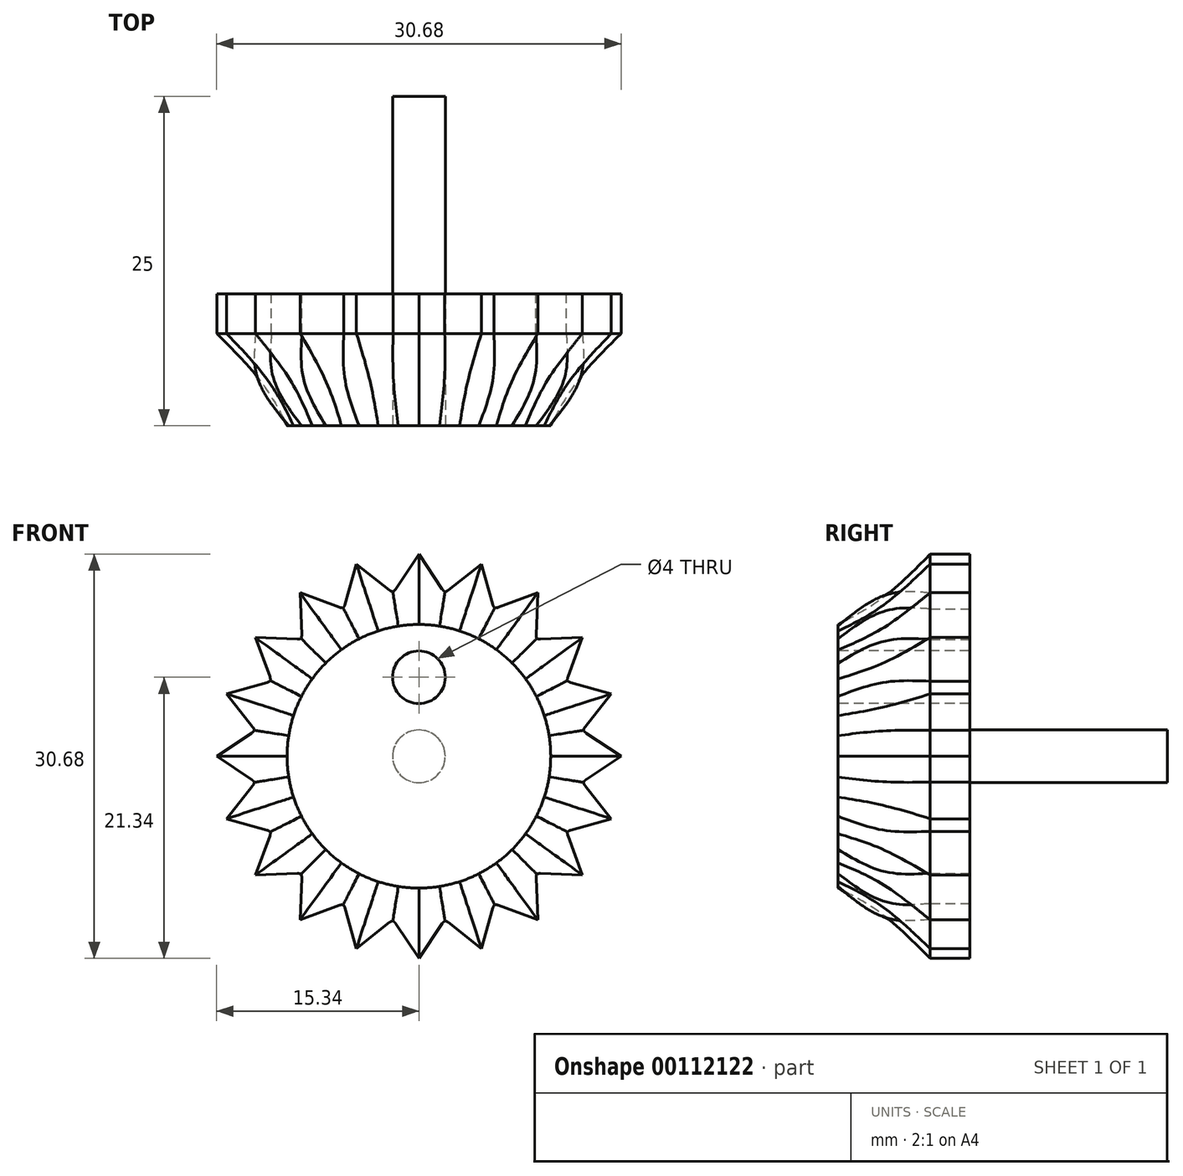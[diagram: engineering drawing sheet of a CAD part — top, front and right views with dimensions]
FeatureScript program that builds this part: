
annotation { "Feature Type Name" : "Feature", "Feature Type Description" : "" }
export const myFeature = defineFeature(function(context is Context, id is Id, definition is map)
    precondition{}
    {
        {
            var Q0;
            Q0=qCreatedBy(makeId("Front.planeOp"),FACE);
            var sketch = newSketch(context, id + "F0", { "sketchPlane" : qUnion([Q0])});
            skCircle(sketch, "E0", {"center": v(0, 0) * mm, "radius": 12.5 * mm, "construction": true});
            skLineSegment(sketch, "E1", {"start": v(-2, 12.34) * mm, "end": v(0, 15.34) * mm});
            skLineSegment(sketch, "E2", {"start": v(0, 15.34) * mm, "end": v(2, 12.34) * mm});
            skLineSegment(sketch, "E3", {"start": v(2, 12.34) * mm, "end": v(-2, 12.34) * mm, "construction": true});
            skLineSegment(sketch, "E4.1.0", {"start": v(-5.72, 11.12) * mm, "end": v(-4.74, 14.59) * mm});
            skLineSegment(sketch, "E4.1.1", {"start": v(-4.74, 14.59) * mm, "end": v(-1.91, 12.35) * mm});
            skLineSegment(sketch, "E4.2.0", {"start": v(-8.87, 8.8) * mm, "end": v(-9.02, 12.4) * mm});
            skLineSegment(sketch, "E4.2.1", {"start": v(-9.02, 12.4) * mm, "end": v(-5.63, 11.16) * mm});
            skLineSegment(sketch, "E4.3.0", {"start": v(-11.16, 5.63) * mm, "end": v(-12.4, 9.02) * mm});
            skLineSegment(sketch, "E4.3.1", {"start": v(-12.4, 9.02) * mm, "end": v(-8.8, 8.87) * mm});
            skLineSegment(sketch, "E4.4.0", {"start": v(-12.35, 1.91) * mm, "end": v(-14.59, 4.74) * mm});
            skLineSegment(sketch, "E4.4.1", {"start": v(-14.59, 4.74) * mm, "end": v(-11.12, 5.72) * mm});
            skLineSegment(sketch, "E4.5.0", {"start": v(-12.34, -2) * mm, "end": v(-15.34, 0) * mm});
            skLineSegment(sketch, "E4.5.1", {"start": v(-15.34, 0) * mm, "end": v(-12.34, 2) * mm});
            skLineSegment(sketch, "E4.6.0", {"start": v(-11.12, -5.72) * mm, "end": v(-14.59, -4.74) * mm});
            skLineSegment(sketch, "E4.6.1", {"start": v(-14.59, -4.74) * mm, "end": v(-12.35, -1.91) * mm});
            skLineSegment(sketch, "E4.7.0", {"start": v(-8.8, -8.87) * mm, "end": v(-12.4, -9.02) * mm});
            skLineSegment(sketch, "E4.7.1", {"start": v(-12.4, -9.02) * mm, "end": v(-11.16, -5.63) * mm});
            skLineSegment(sketch, "E4.8.0", {"start": v(-5.63, -11.16) * mm, "end": v(-9.02, -12.4) * mm});
            skLineSegment(sketch, "E4.8.1", {"start": v(-9.02, -12.4) * mm, "end": v(-8.87, -8.8) * mm});
            skLineSegment(sketch, "E4.9.0", {"start": v(-1.91, -12.35) * mm, "end": v(-4.74, -14.59) * mm});
            skLineSegment(sketch, "E4.9.1", {"start": v(-4.74, -14.59) * mm, "end": v(-5.72, -11.12) * mm});
            skLineSegment(sketch, "E5.1.10.0", {"start": v(2, -12.34) * mm, "end": v(0, -15.34) * mm});
            skLineSegment(sketch, "E5.3.10.0", {"start": v(0, -15.34) * mm, "end": v(-2, -12.34) * mm});
            skLineSegment(sketch, "E6.1.11.0", {"start": v(5.72, -11.12) * mm, "end": v(4.74, -14.59) * mm});
            skLineSegment(sketch, "E6.3.11.0", {"start": v(4.74, -14.59) * mm, "end": v(1.91, -12.35) * mm});
            skLineSegment(sketch, "E7.1.12.0", {"start": v(8.87, -8.8) * mm, "end": v(9.02, -12.4) * mm});
            skLineSegment(sketch, "E7.3.12.0", {"start": v(9.02, -12.4) * mm, "end": v(5.63, -11.16) * mm});
            skLineSegment(sketch, "E7.1.13.0", {"start": v(11.16, -5.63) * mm, "end": v(12.4, -9.02) * mm});
            skLineSegment(sketch, "E7.3.13.0", {"start": v(12.4, -9.02) * mm, "end": v(8.8, -8.87) * mm});
            skLineSegment(sketch, "E8.1.14.0", {"start": v(12.35, -1.91) * mm, "end": v(14.59, -4.74) * mm});
            skLineSegment(sketch, "E8.3.14.0", {"start": v(14.59, -4.74) * mm, "end": v(11.12, -5.72) * mm});
            skLineSegment(sketch, "E8.1.15.0", {"start": v(12.34, 2) * mm, "end": v(15.34, 0) * mm});
            skLineSegment(sketch, "E8.3.15.0", {"start": v(15.34, 0) * mm, "end": v(12.34, -2) * mm});
            skLineSegment(sketch, "E8.1.16.0", {"start": v(11.12, 5.72) * mm, "end": v(14.59, 4.74) * mm});
            skLineSegment(sketch, "E8.3.16.0", {"start": v(14.59, 4.74) * mm, "end": v(12.35, 1.91) * mm});
            skLineSegment(sketch, "E8.1.17.0", {"start": v(8.8, 8.87) * mm, "end": v(12.4, 9.02) * mm});
            skLineSegment(sketch, "E8.3.17.0", {"start": v(12.4, 9.02) * mm, "end": v(11.16, 5.63) * mm});
            skLineSegment(sketch, "E8.1.18.0", {"start": v(5.63, 11.16) * mm, "end": v(9.02, 12.4) * mm});
            skLineSegment(sketch, "E8.3.18.0", {"start": v(9.02, 12.4) * mm, "end": v(8.87, 8.8) * mm});
            skLineSegment(sketch, "E8.1.19.0", {"start": v(1.91, 12.35) * mm, "end": v(4.74, 14.59) * mm});
            skLineSegment(sketch, "E8.3.19.0", {"start": v(4.74, 14.59) * mm, "end": v(5.72, 11.12) * mm});
            skSolve(sketch);
        }
        {
            var Q0;
            Q0=qSketchRegion(id+"F0",true);
            extrude(context, id + "F1", {"entities" : qUnion([Q0]), "depth" : 3 * mm});
        }
        {
            var Q0;
            Q0=makeQuery(id+"F1.opExtrude","CAP_FACE",FACE,{"disambiguationData":[OSD([sQuery(id+"F0.wireOp",EDGE,"fbJdyaIG-X2Uv-iruu-1M7H-KIjKJSGYAYfz"),sQuery(id+"F0.wireOp",EDGE,"E1"),sQuery(id+"F0.wireOp",EDGE,"E2"),sQuery(id+"F0.wireOp",EDGE,"E4.1.0"),sQuery(id+"F0.wireOp",EDGE,"E4.1.1"),sQuery(id+"F0.wireOp",EDGE,"E4.2.0"),sQuery(id+"F0.wireOp",EDGE,"E4.2.1"),sQuery(id+"F0.wireOp",EDGE,"E4.3.0"),sQuery(id+"F0.wireOp",EDGE,"E4.3.1"),sQuery(id+"F0.wireOp",EDGE,"E4.4.0"),sQuery(id+"F0.wireOp",EDGE,"E4.4.1"),sQuery(id+"F0.wireOp",EDGE,"E4.5.0"),sQuery(id+"F0.wireOp",EDGE,"E4.5.1"),sQuery(id+"F0.wireOp",EDGE,"E4.6.0"),sQuery(id+"F0.wireOp",EDGE,"E4.6.1"),sQuery(id+"F0.wireOp",EDGE,"E4.7.0"),sQuery(id+"F0.wireOp",EDGE,"E4.7.1"),sQuery(id+"F0.wireOp",EDGE,"E4.8.0"),sQuery(id+"F0.wireOp",EDGE,"E4.8.1"),sQuery(id+"F0.wireOp",EDGE,"E4.9.0"),sQuery(id+"F0.wireOp",EDGE,"E4.9.1"),sQuery(id+"F0.wireOp",EDGE,"E4.10.0"),sQuery(id+"F0.wireOp",EDGE,"E4.10.1"),sQuery(id+"F0.wireOp",EDGE,"E4.11.0"),sQuery(id+"F0.wireOp",EDGE,"E4.11.1"),sQuery(id+"F0.wireOp",EDGE,"E4.12.0"),sQuery(id+"F0.wireOp",EDGE,"E4.12.1"),sQuery(id+"F0.wireOp",EDGE,"E4.13.0"),sQuery(id+"F0.wireOp",EDGE,"E4.13.1"),sQuery(id+"F0.wireOp",EDGE,"E4.14.0"),sQuery(id+"F0.wireOp",EDGE,"E4.14.1"),sQuery(id+"F0.wireOp",EDGE,"E4.15.0"),sQuery(id+"F0.wireOp",EDGE,"E4.15.1")])],"isStart":true});
            var sketch = newSketch(context, id + "F2", { "sketchPlane" : qUnion([Q0])});
            skCircle(sketch, "E9", {"center": v(0, 0) * mm, "radius": 2 * mm});
            skSolve(sketch);
        }
        {
            var Q0;
            Q0=qSketchRegion(id+"F2",true);
            extrude(context, id + "F3", {"entities" : qUnion([Q0]), "operationType" : NewBodyOperationType.ADD, "depth" : 15 * mm});
        }
        {
            var Q0;
            Q0=makeQuery(id+"F1.opExtrude","CAP_FACE",FACE,{"disambiguationData":[OSD([sQuery(id+"F0.wireOp",EDGE,"E1"),sQuery(id+"F0.wireOp",EDGE,"E2"),sQuery(id+"F0.wireOp",EDGE,"E4.1.0"),sQuery(id+"F0.wireOp",EDGE,"E4.1.1"),sQuery(id+"F0.wireOp",EDGE,"E4.2.0"),sQuery(id+"F0.wireOp",EDGE,"E4.2.1"),sQuery(id+"F0.wireOp",EDGE,"E4.3.0"),sQuery(id+"F0.wireOp",EDGE,"E4.3.1"),sQuery(id+"F0.wireOp",EDGE,"E4.4.0"),sQuery(id+"F0.wireOp",EDGE,"E4.4.1"),sQuery(id+"F0.wireOp",EDGE,"E4.5.0"),sQuery(id+"F0.wireOp",EDGE,"E4.5.1"),sQuery(id+"F0.wireOp",EDGE,"E4.6.0"),sQuery(id+"F0.wireOp",EDGE,"E4.6.1"),sQuery(id+"F0.wireOp",EDGE,"E4.7.0"),sQuery(id+"F0.wireOp",EDGE,"E4.7.1"),sQuery(id+"F0.wireOp",EDGE,"E4.8.0"),sQuery(id+"F0.wireOp",EDGE,"E4.8.1"),sQuery(id+"F0.wireOp",EDGE,"E4.9.0"),sQuery(id+"F0.wireOp",EDGE,"E4.9.1"),sQuery(id+"F0.wireOp",EDGE,"E5.1.10.0"),sQuery(id+"F0.wireOp",EDGE,"E5.3.10.0"),sQuery(id+"F0.wireOp",EDGE,"E6.1.11.0"),sQuery(id+"F0.wireOp",EDGE,"E6.3.11.0"),sQuery(id+"F0.wireOp",EDGE,"E7.1.12.0"),sQuery(id+"F0.wireOp",EDGE,"E7.3.12.0"),sQuery(id+"F0.wireOp",EDGE,"E7.1.13.0"),sQuery(id+"F0.wireOp",EDGE,"E7.3.13.0"),sQuery(id+"F0.wireOp",EDGE,"E8.1.14.0"),sQuery(id+"F0.wireOp",EDGE,"E8.3.14.0"),sQuery(id+"F0.wireOp",EDGE,"E8.1.15.0"),sQuery(id+"F0.wireOp",EDGE,"E8.3.15.0"),sQuery(id+"F0.wireOp",EDGE,"E8.1.16.0"),sQuery(id+"F0.wireOp",EDGE,"E8.3.16.0"),sQuery(id+"F0.wireOp",EDGE,"E8.1.17.0"),sQuery(id+"F0.wireOp",EDGE,"E8.3.17.0"),sQuery(id+"F0.wireOp",EDGE,"E8.1.18.0"),sQuery(id+"F0.wireOp",EDGE,"E8.3.18.0"),sQuery(id+"F0.wireOp",EDGE,"E8.1.19.0"),sQuery(id+"F0.wireOp",EDGE,"E8.3.19.0"),sQuery(id+"F0.wireOp",EDGE,"kuZlPc9k-eGlJ-LJDZ-wCxi-x52hGT55WUVo")])],"isStart":false});
            cPlane(context, id + "F4", {"entities" : qUnion([Q0]), "cplaneType" : CPlaneType.OFFSET, "offset" : 3 * mm, "width" : 150 * mm, "height" : 150 * mm});
        }
        {
            var Q0;
            Q0=qCreatedBy(id+"F4.planeOp",FACE);
            var sketch = newSketch(context, id + "F5", { "sketchPlane" : qUnion([Q0])});
            skCircle(sketch, "E10", {"center": v(0, 0) * mm, "radius": 12.5 * mm});
            skSolve(sketch);
        }
        {
            var Q0;
            Q0=makeQuery(id+"F1.opExtrude","CAP_FACE",FACE,{"disambiguationData":[OSD([sQuery(id+"F0.wireOp",EDGE,"E1"),sQuery(id+"F0.wireOp",EDGE,"E2"),sQuery(id+"F0.wireOp",EDGE,"E4.1.0"),sQuery(id+"F0.wireOp",EDGE,"E4.1.1"),sQuery(id+"F0.wireOp",EDGE,"E4.2.0"),sQuery(id+"F0.wireOp",EDGE,"E4.2.1"),sQuery(id+"F0.wireOp",EDGE,"E4.3.0"),sQuery(id+"F0.wireOp",EDGE,"E4.3.1"),sQuery(id+"F0.wireOp",EDGE,"E4.4.0"),sQuery(id+"F0.wireOp",EDGE,"E4.4.1"),sQuery(id+"F0.wireOp",EDGE,"E4.5.0"),sQuery(id+"F0.wireOp",EDGE,"E4.5.1"),sQuery(id+"F0.wireOp",EDGE,"E4.6.0"),sQuery(id+"F0.wireOp",EDGE,"E4.6.1"),sQuery(id+"F0.wireOp",EDGE,"E4.7.0"),sQuery(id+"F0.wireOp",EDGE,"E4.7.1"),sQuery(id+"F0.wireOp",EDGE,"E4.8.0"),sQuery(id+"F0.wireOp",EDGE,"E4.8.1"),sQuery(id+"F0.wireOp",EDGE,"E4.9.0"),sQuery(id+"F0.wireOp",EDGE,"E4.9.1"),sQuery(id+"F0.wireOp",EDGE,"E5.1.10.0"),sQuery(id+"F0.wireOp",EDGE,"E5.3.10.0"),sQuery(id+"F0.wireOp",EDGE,"E6.1.11.0"),sQuery(id+"F0.wireOp",EDGE,"E6.3.11.0"),sQuery(id+"F0.wireOp",EDGE,"E7.1.12.0"),sQuery(id+"F0.wireOp",EDGE,"E7.3.12.0"),sQuery(id+"F0.wireOp",EDGE,"E7.1.13.0"),sQuery(id+"F0.wireOp",EDGE,"E7.3.13.0"),sQuery(id+"F0.wireOp",EDGE,"E8.1.14.0"),sQuery(id+"F0.wireOp",EDGE,"E8.3.14.0"),sQuery(id+"F0.wireOp",EDGE,"E8.1.15.0"),sQuery(id+"F0.wireOp",EDGE,"E8.3.15.0"),sQuery(id+"F0.wireOp",EDGE,"E8.1.16.0"),sQuery(id+"F0.wireOp",EDGE,"E8.3.16.0"),sQuery(id+"F0.wireOp",EDGE,"E8.1.17.0"),sQuery(id+"F0.wireOp",EDGE,"E8.3.17.0"),sQuery(id+"F0.wireOp",EDGE,"E8.1.18.0"),sQuery(id+"F0.wireOp",EDGE,"E8.3.18.0"),sQuery(id+"F0.wireOp",EDGE,"E8.1.19.0"),sQuery(id+"F0.wireOp",EDGE,"E8.3.19.0"),sQuery(id+"F0.wireOp",EDGE,"kuZlPc9k-eGlJ-LJDZ-wCxi-x52hGT55WUVo")])],"isStart":false});
            var sketch = newSketch(context, id + "F6", { "sketchPlane" : qUnion([Q0])});
            skLineSegment(sketch, "E11.0.0", {"start": v(-4.74, -14.59) * mm, "end": v(-1.96, -12.4) * mm});
            skLineSegment(sketch, "E11.0.1", {"start": v(-1.96, -12.4) * mm, "end": v(0, -15.34) * mm});
            skLineSegment(sketch, "E11.0.2", {"start": v(0, -15.34) * mm, "end": v(1.96, -12.4) * mm});
            skLineSegment(sketch, "E11.0.3", {"start": v(1.96, -12.4) * mm, "end": v(4.74, -14.59) * mm});
            skLineSegment(sketch, "E11.0.4", {"start": v(4.74, -14.59) * mm, "end": v(5.7, -11.18) * mm});
            skLineSegment(sketch, "E11.0.5", {"start": v(5.7, -11.18) * mm, "end": v(9.02, -12.4) * mm});
            skLineSegment(sketch, "E11.0.6", {"start": v(9.02, -12.4) * mm, "end": v(8.87, -8.87) * mm});
            skLineSegment(sketch, "E11.0.7", {"start": v(8.87, -8.87) * mm, "end": v(12.4, -9.02) * mm});
            skLineSegment(sketch, "E11.0.8", {"start": v(12.4, -9.02) * mm, "end": v(11.18, -5.7) * mm});
            skLineSegment(sketch, "E11.0.9", {"start": v(11.18, -5.7) * mm, "end": v(14.59, -4.74) * mm});
            skLineSegment(sketch, "E11.0.10", {"start": v(14.59, -4.74) * mm, "end": v(12.4, -1.96) * mm});
            skLineSegment(sketch, "E11.0.11", {"start": v(12.4, -1.96) * mm, "end": v(15.34, 0) * mm});
            skLineSegment(sketch, "E11.0.12", {"start": v(15.34, 0) * mm, "end": v(12.4, 1.96) * mm});
            skLineSegment(sketch, "E11.0.13", {"start": v(12.4, 1.96) * mm, "end": v(14.59, 4.74) * mm});
            skLineSegment(sketch, "E11.0.14", {"start": v(14.59, 4.74) * mm, "end": v(11.18, 5.7) * mm});
            skLineSegment(sketch, "E11.0.15", {"start": v(11.18, 5.7) * mm, "end": v(12.4, 9.02) * mm});
            skLineSegment(sketch, "E11.0.16", {"start": v(12.4, 9.02) * mm, "end": v(8.87, 8.87) * mm});
            skLineSegment(sketch, "E11.0.17", {"start": v(8.87, 8.87) * mm, "end": v(9.02, 12.4) * mm});
            skLineSegment(sketch, "E11.0.18", {"start": v(9.02, 12.4) * mm, "end": v(5.7, 11.18) * mm});
            skLineSegment(sketch, "E11.0.19", {"start": v(5.7, 11.18) * mm, "end": v(4.74, 14.59) * mm});
            skLineSegment(sketch, "E11.0.20", {"start": v(4.74, 14.59) * mm, "end": v(1.96, 12.4) * mm});
            skLineSegment(sketch, "E11.0.21", {"start": v(1.96, 12.4) * mm, "end": v(0, 15.34) * mm});
            skLineSegment(sketch, "E11.0.22", {"start": v(0, 15.34) * mm, "end": v(-1.96, 12.4) * mm});
            skLineSegment(sketch, "E11.0.23", {"start": v(-1.96, 12.4) * mm, "end": v(-4.74, 14.59) * mm});
            skLineSegment(sketch, "E11.0.24", {"start": v(-4.74, 14.59) * mm, "end": v(-5.7, 11.18) * mm});
            skLineSegment(sketch, "E11.0.25", {"start": v(-5.7, 11.18) * mm, "end": v(-9.02, 12.4) * mm});
            skLineSegment(sketch, "E11.0.26", {"start": v(-9.02, 12.4) * mm, "end": v(-8.87, 8.87) * mm});
            skLineSegment(sketch, "E11.0.27", {"start": v(-8.87, 8.87) * mm, "end": v(-12.4, 9.02) * mm});
            skLineSegment(sketch, "E11.0.28", {"start": v(-12.4, 9.02) * mm, "end": v(-11.18, 5.7) * mm});
            skLineSegment(sketch, "E11.0.29", {"start": v(-11.18, 5.7) * mm, "end": v(-14.59, 4.74) * mm});
            skLineSegment(sketch, "E11.0.30", {"start": v(-14.59, 4.74) * mm, "end": v(-12.4, 1.96) * mm});
            skLineSegment(sketch, "E11.0.31", {"start": v(-12.4, 1.96) * mm, "end": v(-15.34, 0) * mm});
            skLineSegment(sketch, "E11.0.32", {"start": v(-15.34, 0) * mm, "end": v(-12.4, -1.96) * mm});
            skLineSegment(sketch, "E11.0.33", {"start": v(-12.4, -1.96) * mm, "end": v(-14.59, -4.74) * mm});
            skLineSegment(sketch, "E11.0.34", {"start": v(-14.59, -4.74) * mm, "end": v(-11.18, -5.7) * mm});
            skLineSegment(sketch, "E11.0.35", {"start": v(-11.18, -5.7) * mm, "end": v(-12.4, -9.02) * mm});
            skLineSegment(sketch, "E11.0.36", {"start": v(-12.4, -9.02) * mm, "end": v(-8.87, -8.87) * mm});
            skLineSegment(sketch, "E11.0.37", {"start": v(-8.87, -8.87) * mm, "end": v(-9.02, -12.4) * mm});
            skLineSegment(sketch, "E11.0.38", {"start": v(-9.02, -12.4) * mm, "end": v(-5.7, -11.18) * mm});
            skLineSegment(sketch, "E11.0.39", {"start": v(-5.7, -11.18) * mm, "end": v(-4.74, -14.59) * mm});
            skSolve(sketch);
        }
        {
            var Q0;
            Q0=qCreatedBy(id+"F4.planeOp",FACE);
            cPlane(context, id + "F7", {"entities" : qUnion([Q0]), "cplaneType" : CPlaneType.OFFSET, "offset" : 4 * mm, "width" : 150 * mm, "height" : 150 * mm});
        }
        {
            var Q0;
            Q0=qCreatedBy(id+"F7.planeOp",FACE);
            var sketch = newSketch(context, id + "F8", { "sketchPlane" : qUnion([Q0])});
            skCircle(sketch, "E12", {"center": v(0, 0) * mm, "radius": 10 * mm});
            skSolve(sketch);
        }
        {
            var Q1;
            Q1 = qSketchRegion(id + "F6", true);
            var Q2;
            Q2 = qSketchRegion(id + "F5", true);
            var Q3;
            Q3 = qSketchRegion(id + "F8", true);
            loft(context, id + "F9", {"operationType" : NewBodyOperationType.ADD, "sheetProfilesArray" : [{ "sheetProfileEntities" : qUnion([Q1]) }, { "sheetProfileEntities" : qUnion([Q2]) }, { "sheetProfileEntities" : qUnion([Q3]) }]});
        }
        {
            var Q0;
            Q0=makeQuery(id+"F9.opLoft","CAP_FACE",FACE,{"disambiguationData":[OSD([makeQuery(id+"F8.imprint","IMPRINT",FACE,{"disambiguationData":[TD([[makeQuery(id+"F8.imprint","IMPRINT",EDGE,{"derivedFrom":sQuery(id+"F8.wireOp",EDGE,"E12")}),1.0]])]})])],"isStart":true});
            var sketch = newSketch(context, id + "F10", { "sketchPlane" : qUnion([Q0])});
            skCircle(sketch, "E13", {"center": v(0, 6) * mm, "radius": 2 * mm});
            skSolve(sketch);
        }
        {
            var Q0;
            Q0=makeQuery(id+"F10.imprint","IMPRINT",FACE,{"disambiguationData":[TD([[makeQuery(id+"F10.imprint","IMPRINT",EDGE,{"derivedFrom":sQuery(id+"F10.wireOp",EDGE,"E13")}),1.0]])]});
            extrude(context, id + "F11", {"entities" : qUnion([Q0]), "operationType" : NewBodyOperationType.REMOVE, "endBound" : BoundingType.UP_TO_NEXT, "oppositeDirection" : true, "depth" : 25 * mm});
        }
    });
